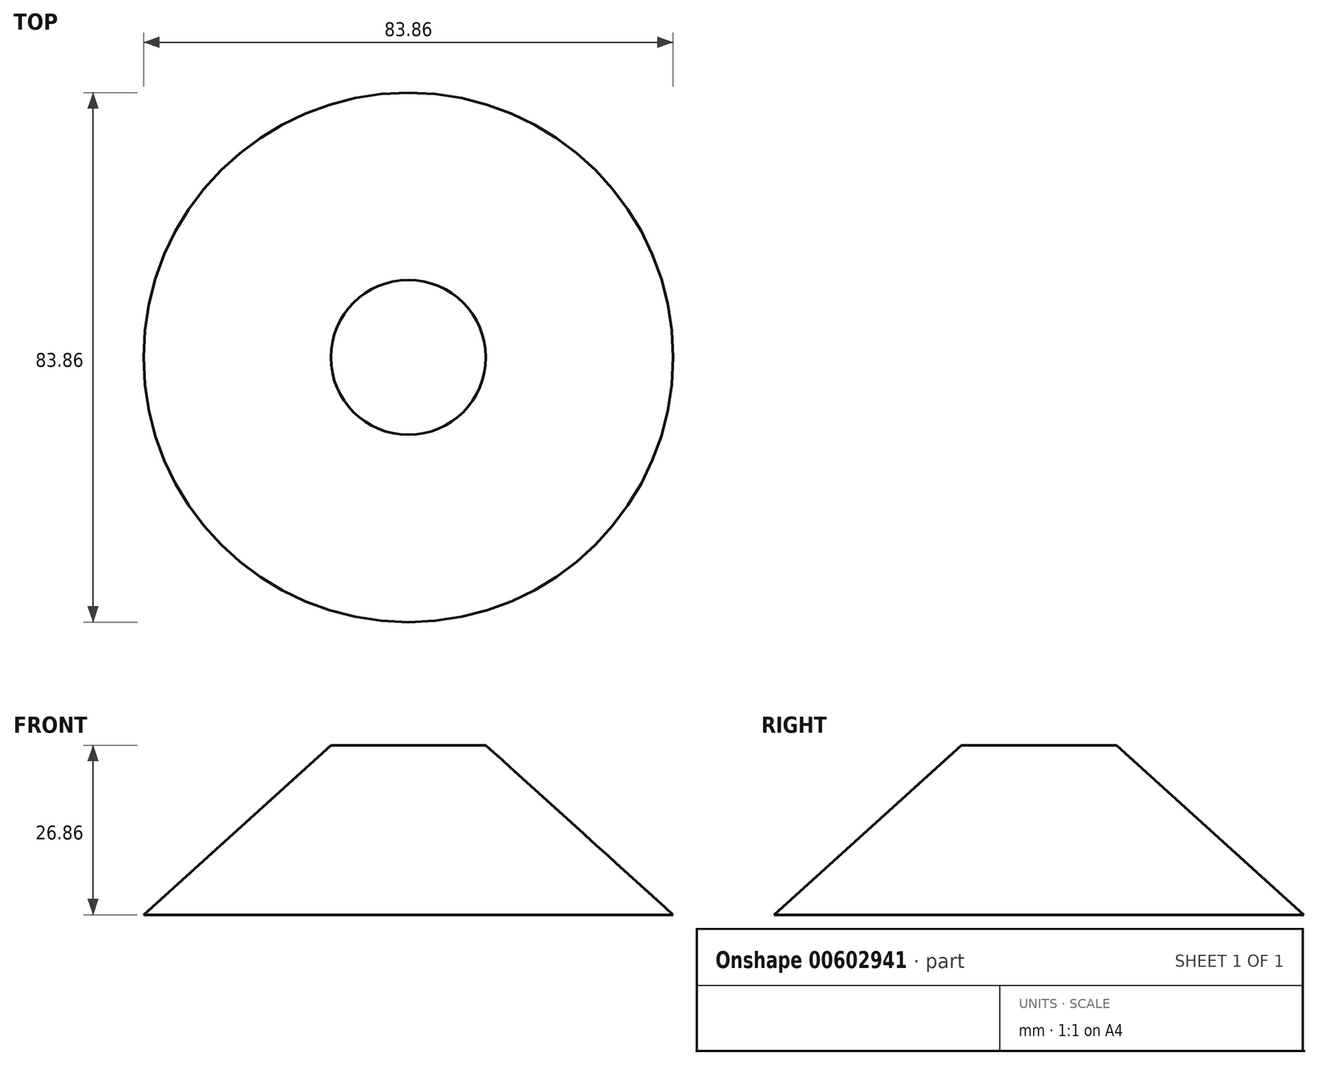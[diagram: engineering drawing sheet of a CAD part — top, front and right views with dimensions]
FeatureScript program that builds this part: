
annotation { "Feature Type Name" : "Feature", "Feature Type Description" : "" }
export const myFeature = defineFeature(function(context is Context, id is Id, definition is map)
    precondition{}
    {
        {
            var Q0;
            Q0=qCreatedBy(makeId("Front.planeOp"),FACE);
            var sketch = newSketch(context, id + "F0", { "sketchPlane" : qUnion([Q0])});
            skLineSegment(sketch, "E0", {"start": v(12.26, 26.86) * mm, "end": v(0, 26.86) * mm});
            skLineSegment(sketch, "E1", {"start": v(0, 26.86) * mm, "end": v(0, 0) * mm});
            skLineSegment(sketch, "E2", {"start": v(0, 0) * mm, "end": v(12.5, 0) * mm});
            skLineSegment(sketch, "E3", {"start": v(12.26, 26.86) * mm, "end": v(41.93, 0) * mm});
            skLineSegment(sketch, "E4", {"start": v(41.93, 0) * mm, "end": v(12.5, 0) * mm});
            skSolve(sketch);
        }
        {
            var Q0;
            Q0=makeQuery(id+"F0.imprint","IMPRINT",FACE,{"disambiguationData":[TD([[makeQuery(id+"F0.imprint","IMPRINT",EDGE,{"derivedFrom":sQuery(id+"F0.wireOp",EDGE,"E0")}),1.0]])]});
            var Q1;
            Q1=sQuery(id+"F0.wireOp",EDGE,"E1");
            revolve(context, id + "F1", {"entities" : qUnion([Q0]), "axis" : qUnion([Q1]), "revolveType" : RevolveType.FULL});
        }
        {
            var Q0;
            Q0=makeQuery(id+"F1.opRevolve","SWEPT_FACE",FACE,{"disambiguationData":[OSD([sQuery(id+"F0.wireOp",EDGE,"E0")])]});
            var sketch = newSketch(context, id + "F2", { "sketchPlane" : qUnion([Q0])});
            skCircle(sketch, "E5", {"center": v(0, 0) * mm, "radius": 8.86 * mm});
            skSolve(sketch);
        }
        {
            var Q0;
            Q0=sQuery(id+"F2.wireOp",EDGE,"E5");
            extrude(context, id + "F3", {"bodyType" : ToolBodyType.SURFACE, "surfaceEntities" : qUnion([Q0]), "depth" : 5 * mm, "offsetDistance" : 25.4 * mm});
        }
    });
